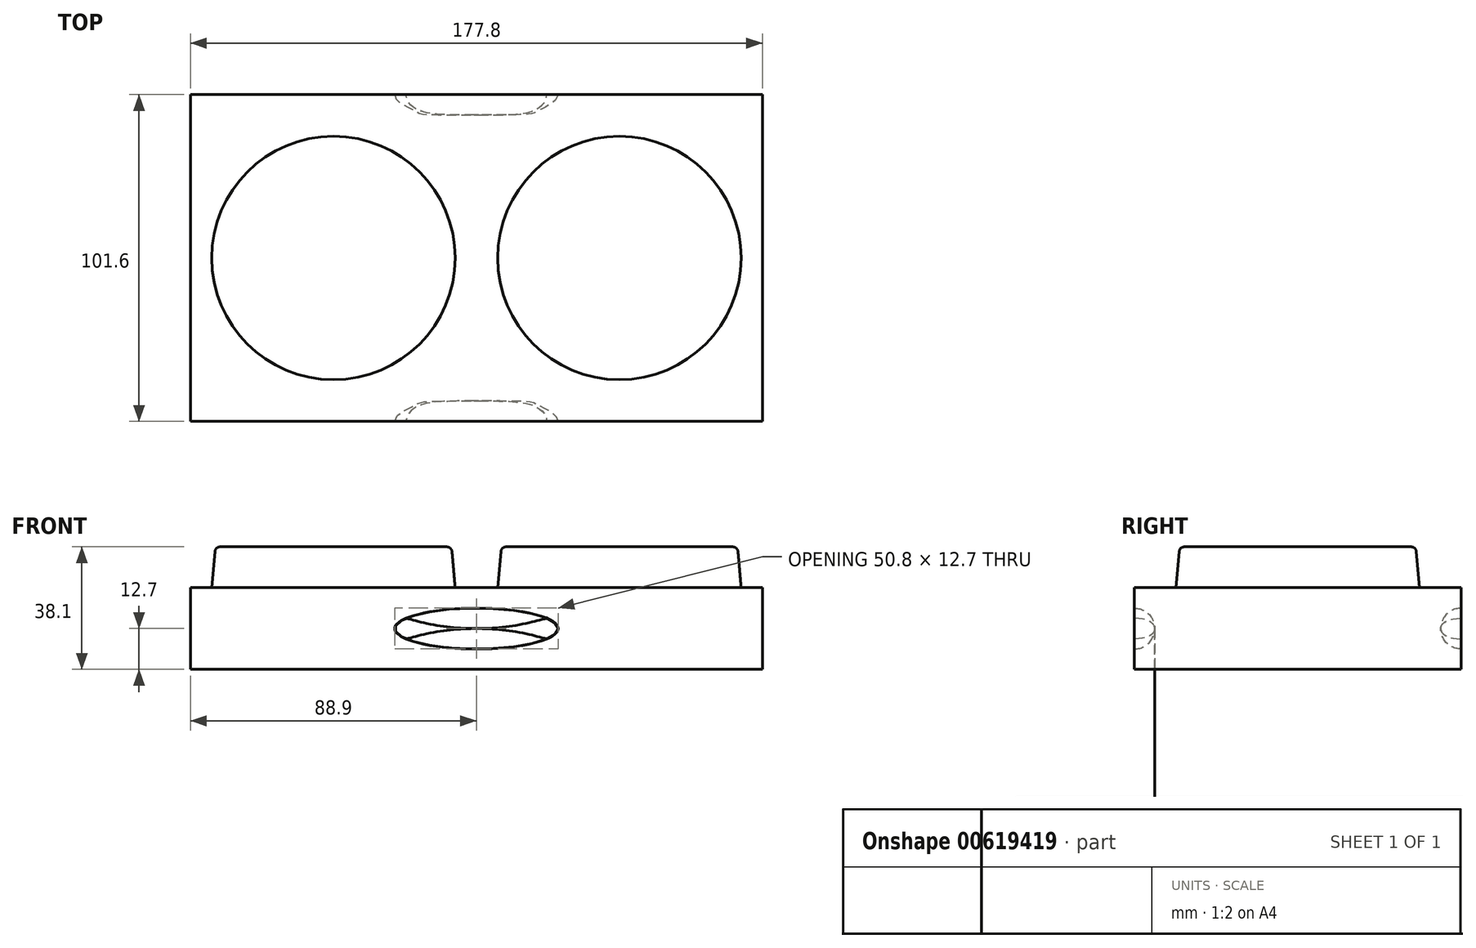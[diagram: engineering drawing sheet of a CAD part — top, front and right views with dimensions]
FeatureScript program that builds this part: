
annotation { "Feature Type Name" : "Feature", "Feature Type Description" : "" }
export const myFeature = defineFeature(function(context is Context, id is Id, definition is map)
    precondition{}
    {
        {
            var Q0;
            Q0=qCreatedBy(makeId("Top.planeOp"),FACE);
            var sketch = newSketch(context, id + "F0", { "sketchPlane" : qUnion([Q0])});
            skLineSegment(sketch, "E0.bottom", {"start": v(-88.9, 50.8) * mm, "end": v(88.9, 50.8) * mm});
            skLineSegment(sketch, "E0.top", {"start": v(-88.9, -50.8) * mm, "end": v(88.9, -50.8) * mm});
            skLineSegment(sketch, "E0.left", {"start": v(-88.9, 50.8) * mm, "end": v(-88.9, -50.8) * mm});
            skLineSegment(sketch, "E0.right", {"start": v(88.9, 50.8) * mm, "end": v(88.9, -50.8) * mm});
            skSolve(sketch);
        }
        {
            var Q0;
            Q0=qSketchRegion(id+"F0",true);
            extrude(context, id + "F1", {"entities" : qUnion([Q0]), "depth" : 25.4 * mm, "offsetDistance" : 25.4 * mm});
        }
        {
            var Q0;
            Q0=makeQuery(id+"F1.opExtrude","CAP_FACE",FACE,{"disambiguationData":[OSD([sQuery(id+"F0.wireOp",EDGE,"E0.bottom"),sQuery(id+"F0.wireOp",EDGE,"E0.top"),sQuery(id+"F0.wireOp",EDGE,"E0.left"),sQuery(id+"F0.wireOp",EDGE,"E0.right")])],"isStart":false});
            var sketch = newSketch(context, id + "F2", { "sketchPlane" : qUnion([Q0])});
            skCircle(sketch, "E1", {"center": v(-44.45, 0) * mm, "radius": 37.85 * mm});
            skCircle(sketch, "E2", {"center": v(44.45, 0) * mm, "radius": 37.85 * mm});
            skSolve(sketch);
        }
        {
            var Q0;
            Q0=qSketchRegion(id+"F2",true);
            extrude(context, id + "F3", {"entities" : qUnion([Q0]), "operationType" : NewBodyOperationType.ADD, "depth" : 12.7 * mm, "offsetDistance" : 25.4 * mm, "hasDraft" : true, "draftAngle" : 5 * degree, "draftPullDirection" : true});
        }
        {
            var Q0;
            Q0=makeQuery(id+"F3.opExtrude","CAP_EDGE",EDGE,{"disambiguationData":[OSD([sQuery(id+"F2.wireOp",EDGE,"E1")])],"isStart":false});
            var Q1;
            Q1=makeQuery(id+"F3.opExtrude","CAP_EDGE",EDGE,{"disambiguationData":[OSD([sQuery(id+"F2.wireOp",EDGE,"E2")])],"isStart":false});
            fillet(context, id + "F4", {"entities" : qUnion([Q0, Q1]), "radius" : 1.59 * mm, "tangentPropagation" : true, "allowEdgeOverflow" : false});
        }
        {
            var Q0;
            Q0=makeQuery(id+"F1.opExtrude","SWEPT_FACE",FACE,{"disambiguationData":[OSD([sQuery(id+"F0.wireOp",EDGE,"E0.top")])]});
            var sketch = newSketch(context, id + "F5", { "sketchPlane" : qUnion([Q0])});
            skEllipse(sketch, "E3", {"center": v(0, 12.7) * mm, "majorRadius": 25.4 * mm, "minorRadius": 6.35 * mm, "majorAxis": v(1, 0)});
            skSolve(sketch);
        }
        {
            var Q0;
            Q0=qSketchRegion(id+"F5",true);
            extrude(context, id + "F6", {"entities" : qUnion([Q0]), "operationType" : NewBodyOperationType.REMOVE, "oppositeDirection" : true, "depth" : 6.35 * mm, "offsetDistance" : 25.4 * mm});
        }
        {
            var Q0;
            Q0=makeQuery(id+"F6.boolean.opBoolean","COPY",EDGE,{"derivedFrom":makeQuery(id+"F6.opExtrude","CAP_EDGE",EDGE,{"disambiguationData":[OSD([sQuery(id+"F5.wireOp",EDGE,"E3")])],"isStart":false})});
            fillet(context, id + "F7", {"entities" : qUnion([Q0]), "radius" : 6.35 * mm, "tangentPropagation" : true, "allowEdgeOverflow" : false});
        }
        {
            var Q0;
            Q0=makeQuery(id+"F1.opExtrude","SWEPT_FACE",FACE,{"disambiguationData":[OSD([sQuery(id+"F0.wireOp",EDGE,"E0.bottom")])]});
            var sketch = newSketch(context, id + "F8", { "sketchPlane" : qUnion([Q0])});
            skEllipse(sketch, "E4", {"center": v(0, 12.7) * mm, "majorRadius": 25.4 * mm, "minorRadius": 6.35 * mm, "majorAxis": v(1, 0)});
            skSolve(sketch);
        }
        {
            var Q0;
            Q0=qSketchRegion(id+"F8",true);
            extrude(context, id + "F9", {"entities" : qUnion([Q0]), "operationType" : NewBodyOperationType.REMOVE, "oppositeDirection" : true, "depth" : 6.35 * mm, "offsetDistance" : 25.4 * mm});
        }
        {
            var Q0;
            Q0=makeQuery(id+"F9.boolean.opBoolean","COPY",EDGE,{"derivedFrom":makeQuery(id+"F9.opExtrude","CAP_EDGE",EDGE,{"disambiguationData":[OSD([sQuery(id+"F8.wireOp",EDGE,"E4")])],"isStart":false})});
            fillet(context, id + "F10", {"entities" : qUnion([Q0]), "radius" : 6.35 * mm, "tangentPropagation" : true, "allowEdgeOverflow" : false});
        }
    });
